# Revit family: Haworth_Masters_Lateral_Attached
name_source: partatom
category: Furniture Systems
revit_build: Autodesk Revit 2018 (Build: 20170223_1515(x64)
units: mm (PartAtom-declared; Revit-internal decimal feet)

## family parameters
Always vertical = Yes
Cut with Voids When Loaded = No
OmniClass Number = 23.40.70.14.64.21
OmniClass Title = Systems Furniture
Part Type = Normal
Room Calculation Point = No
Round Connector Dimension = Use Diameter
Shared = No
Work Plane-Based = No

## types (2) — shared parameters
Actual Depth = 23"
Actual Height = 21 1/2"
Assembly Code = E2020200
Attached = Yes
Back Edge Of Top = 4"
Bar Pull = No
Base Clearance = 0"
Classic Pull = Yes
Depth 18 or 18.75 = No
Depth 23 or 23.75 = Yes
Description = Haworth - Masters Lateral - Attached
Drawer 1 Height = 13"
Drawer 2 Height = 6 1/2"
Drawer 3 Offset = 1/8"
Finger Pull = No
Finished Back = No
Linear Pull = No
Manufacturer = Haworth
Max Width = 42"
Max. Depth = 23 3/4"
Max. Height = 28"
Min Width = 24"
Min. Depth = 18"
Min. Height = 15 3/16"
Model = Haworth - Masters Lateral - Attached
One And A Half High = Yes
One High = No
Revision Number = 3
Size = Verify Final Dim. w/ Haworth
Standard Depths = 18, 18.75, 23, 23.75 in
Standard Widths = 30, 36 in
Sustainability Info = http://www.haworth.com
Top Drawer = Yes
Two High = No
URL = www.haworth.com
URL - Product = http://www.haworth.com
Warranty = http://www.haworth.com

## per-type parameters (varying)
| type | Actual Width | Bar Pull Length | Cabinet Finish | Custom Size | Drawer Finish | Pull Finish | Width |
| Attached | 42" | 36" | Haworth _ Laminate _ Undecided _ Storage | Yes | Haworth _ Laminate _ Undecided _ Storage | Haworth _ Metal _ Chrome | 42" |
| Attached - 30w | 30" | 24" | Haworth _ Laminate _ Grey Elm | No | Haworth _ Laminate _ Grey Elm | <By Category> | 30" |

## geometry (parser evidence)
native form markers: Sweep x6
no freeform markers — native parametric forms only
